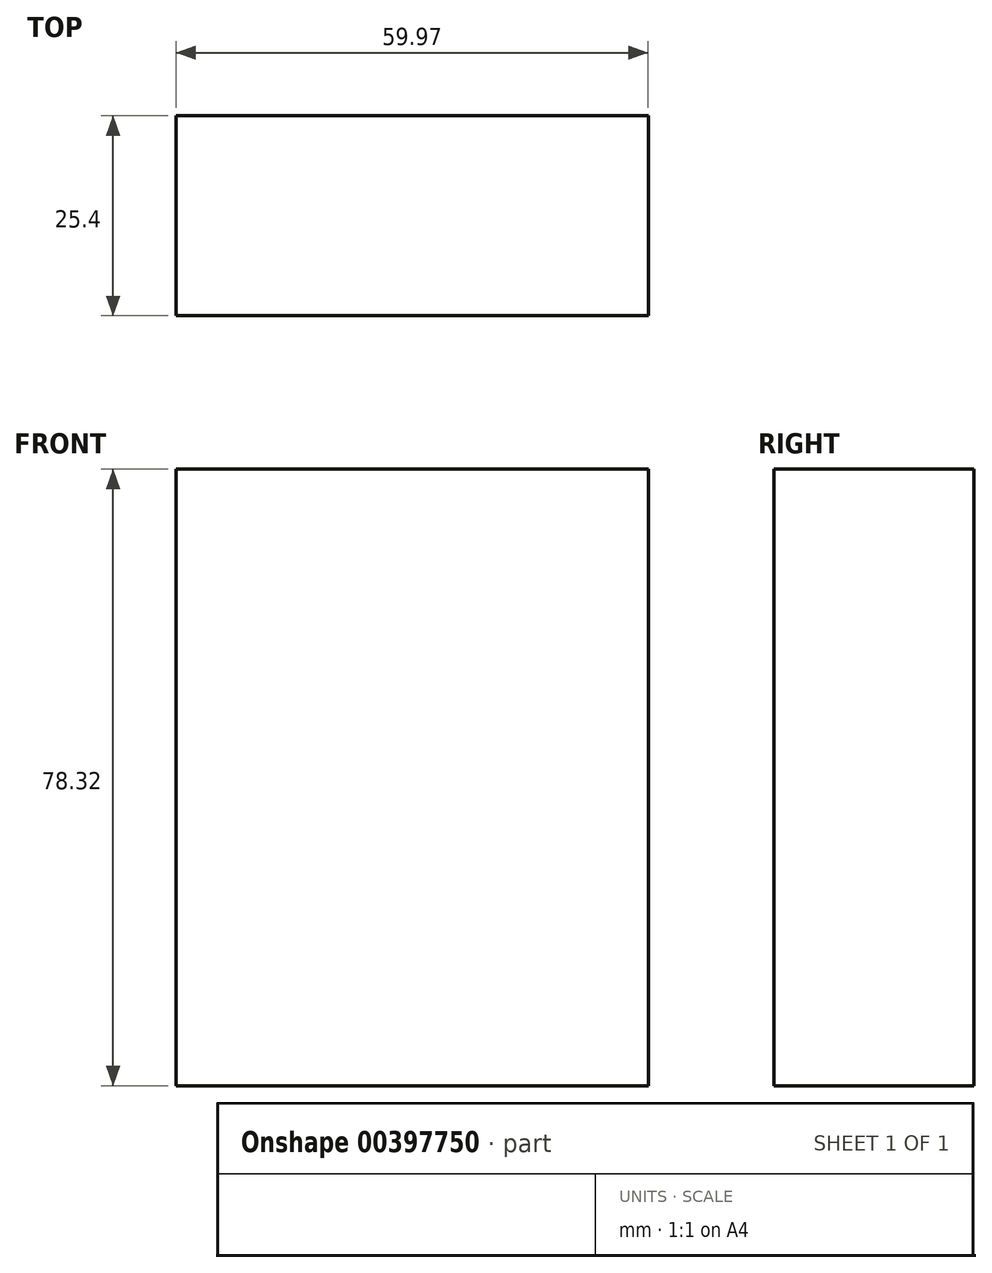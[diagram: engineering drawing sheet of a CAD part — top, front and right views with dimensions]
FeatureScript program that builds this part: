
annotation { "Feature Type Name" : "Feature", "Feature Type Description" : "" }
export const myFeature = defineFeature(function(context is Context, id is Id, definition is map)
    precondition{}
    {
        {
            var Q0;
            Q0=qCreatedBy(makeId("Front.planeOp"),FACE);
            var sketch = newSketch(context, id + "F0", { "sketchPlane" : qUnion([Q0])});
            skLineSegment(sketch, "E0.bottom", {"start": v(-69.75, 66.72) * mm, "end": v(-9.78, 66.72) * mm});
            skLineSegment(sketch, "E0.top", {"start": v(-69.75, -11.6) * mm, "end": v(-9.78, -11.6) * mm});
            skLineSegment(sketch, "E0.left", {"start": v(-69.75, 66.72) * mm, "end": v(-69.75, -11.6) * mm});
            skLineSegment(sketch, "E0.right", {"start": v(-9.78, 66.72) * mm, "end": v(-9.78, -11.6) * mm});
            skSolve(sketch);
        }
        {
            var Q0;
            Q0=makeQuery(id+"F0.imprint","IMPRINT",FACE,{"disambiguationData":[TD([[makeQuery(id+"F0.imprint","IMPRINT",EDGE,{"derivedFrom":sQuery(id+"F0.wireOp",EDGE,"E0.bottom")}),-1.0]])]});
            extrude(context, id + "F1", {"entities" : qUnion([Q0]), "depth" : 25.4 * mm});
        }
    });
